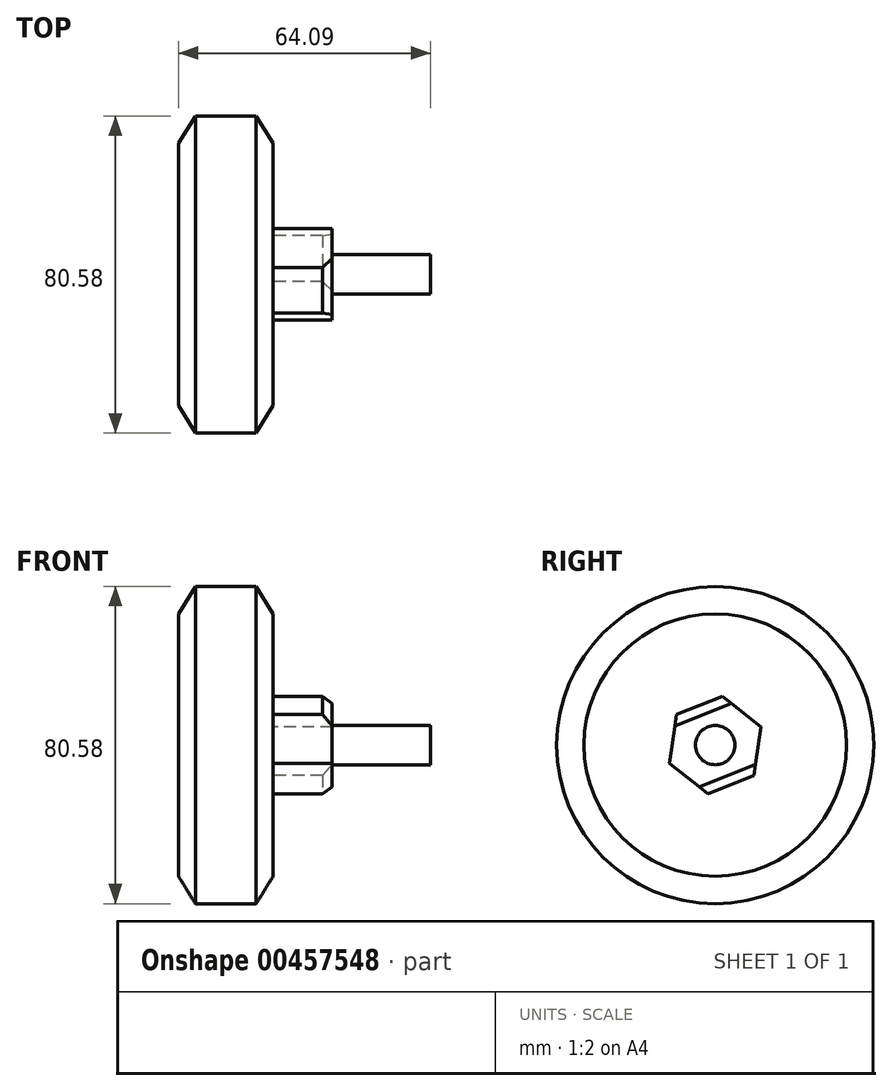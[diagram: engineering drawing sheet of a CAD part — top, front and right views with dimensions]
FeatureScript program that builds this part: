
annotation { "Feature Type Name" : "Feature", "Feature Type Description" : "" }
export const myFeature = defineFeature(function(context is Context, id is Id, definition is map)
    precondition{}
    {
        {
            var Q0;
            Q0=qCreatedBy(makeId("Front.planeOp"),FACE);
            var sketch = newSketch(context, id + "F0", { "sketchPlane" : qUnion([Q0])});
            skLineSegment(sketch, "E0", {"start": v(0, 0) * mm, "end": v(-24.95, 0) * mm});
            skLineSegment(sketch, "E1", {"start": v(-24.95, 0) * mm, "end": v(-24.95, 33.33) * mm});
            skLineSegment(sketch, "E2", {"start": v(-24.95, 33.33) * mm, "end": v(-20.6, 40.29) * mm});
            skLineSegment(sketch, "E3", {"start": v(-12.9, 40.29) * mm, "end": v(-12.9, 0) * mm, "construction": true});
            skLineSegment(sketch, "E4.MirrorCS", {"start": v(-0.86, 0) * mm, "end": v(-0.86, 33.33) * mm});
            skLineSegment(sketch, "E5.MirrorCS", {"start": v(-0.86, 33.33) * mm, "end": v(-5.2, 40.29) * mm});
            skLineSegment(sketch, "E6", {"start": v(-20.6, 40.29) * mm, "end": v(-5.2, 40.29) * mm});
            skLineSegment(sketch, "E7", {"start": v(-24.95, 0) * mm, "end": v(-41.48, 0) * mm, "construction": true});
            skSolve(sketch);
        }
        {
            var Q0;
            Q0 = qSketchRegion(id + "F0", true);
            var Q1;
            Q1=sQuery(id+"F0.wireOp",EDGE,"E7");
            revolve(context, id + "F1", {"entities" : qUnion([Q0]), "axis" : qUnion([Q1]), "revolveType" : RevolveType.FULL});
        }
        {
            var Q0;
            Q0=makeQuery(id+"F1.opRevolve","SWEPT_FACE",FACE,{"disambiguationData":[OSD([sQuery(id+"F0.wireOp",EDGE,"E4.MirrorCS")])]});
            var sketch = newSketch(context, id + "F2", { "sketchPlane" : qUnion([Q0])});
            skCircle(sketch, "E8.cCircle", {"center": v(0, 0) * mm, "radius": 12.5 * mm, "construction": true});
            skLineSegment(sketch, "E8.0", {"start": v(11.61, 4.63) * mm, "end": v(9.81, -7.74) * mm});
            skLineSegment(sketch, "E8.1", {"start": v(9.81, -7.74) * mm, "end": v(-1.8, -12.37) * mm});
            skLineSegment(sketch, "E8.2", {"start": v(-1.8, -12.37) * mm, "end": v(-11.61, -4.63) * mm});
            skLineSegment(sketch, "E8.3", {"start": v(-11.61, -4.63) * mm, "end": v(-9.81, 7.74) * mm});
            skLineSegment(sketch, "E8.4", {"start": v(-9.81, 7.74) * mm, "end": v(1.8, 12.37) * mm});
            skLineSegment(sketch, "E8.5", {"start": v(1.8, 12.37) * mm, "end": v(11.61, 4.63) * mm});
            skSolve(sketch);
        }
        {
            var Q0;
            Q0 = qSketchRegion(id + "F2", true);
            extrude(context, id + "F3", {"entities" : qUnion([Q0]), "operationType" : NewBodyOperationType.ADD, "depth" : 15 * mm});
        }
        {
            var Q0;
            Q0=makeQuery(id+"F3.opExtrude","CAP_FACE",FACE,{"disambiguationData":[OSD([sQuery(id+"F2.wireOp",EDGE,"E8.0"),sQuery(id+"F2.wireOp",EDGE,"E8.1"),sQuery(id+"F2.wireOp",EDGE,"E8.2"),sQuery(id+"F2.wireOp",EDGE,"E8.3"),sQuery(id+"F2.wireOp",EDGE,"E8.4"),sQuery(id+"F2.wireOp",EDGE,"E8.5")])],"isStart":false});
            var sketch = newSketch(context, id + "F4", { "sketchPlane" : qUnion([Q0])});
            skCircle(sketch, "E9", {"center": v(0, 0) * mm, "radius": 5 * mm});
            skSolve(sketch);
        }
        {
            var Q0;
            Q0 = qSketchRegion(id + "F4", true);
            extrude(context, id + "F5", {"entities" : qUnion([Q0]), "operationType" : NewBodyOperationType.ADD, "depth" : 25 * mm});
        }
        {
            var Q0;
            Q0=makeQuery(id+"F3.opExtrude","CAP_EDGE",EDGE,{"disambiguationData":[OSD([sQuery(id+"F2.wireOp",EDGE,"E8.1")])],"isStart":false});
            var Q1;
            Q1=makeQuery(id+"F3.opExtrude","CAP_EDGE",EDGE,{"disambiguationData":[OSD([sQuery(id+"F2.wireOp",EDGE,"E8.4")])],"isStart":false});
            chamfer(context, id + "F6", {"entities" : qUnion([Q0, Q1]), "width" : 2.5 * mm, "tangentPropagation" : true});
        }
    });
